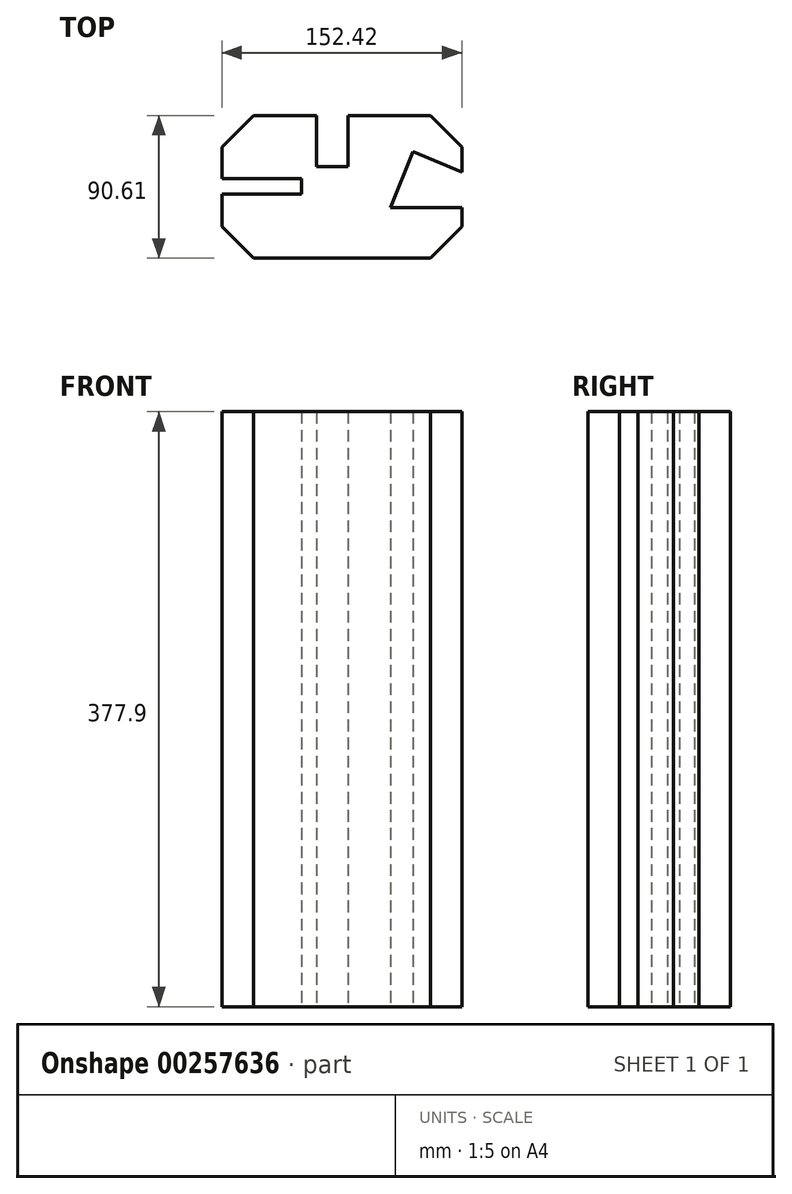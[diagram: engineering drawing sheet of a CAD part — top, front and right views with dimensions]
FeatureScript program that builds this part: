
annotation { "Feature Type Name" : "Feature", "Feature Type Description" : "" }
export const myFeature = defineFeature(function(context is Context, id is Id, definition is map)
    precondition{}
    {
        {
            var Q0;
            Q0=qCreatedBy(makeId("Top.planeOp"),FACE);
            var sketch = newSketch(context, id + "F0", { "sketchPlane" : qUnion([Q0])});
            skLineSegment(sketch, "E0", {"start": v(-44.72, -55.3) * mm, "end": v(67.68, -55.3) * mm});
            skLineSegment(sketch, "E1", {"start": v(67.68, -55.3) * mm, "end": v(87.7, -35.28) * mm});
            skLineSegment(sketch, "E2", {"start": v(-44.72, -55.3) * mm, "end": v(-64.73, -35.28) * mm});
            skLineSegment(sketch, "E3", {"start": v(87.7, -35.28) * mm, "end": v(87.7, -23.28) * mm});
            skLineSegment(sketch, "E4", {"start": v(87.7, -23.28) * mm, "end": v(42.4, -23.28) * mm});
            skLineSegment(sketch, "E5", {"start": v(42.4, -23.28) * mm, "end": v(56.81, 12.41) * mm});
            skLineSegment(sketch, "E6", {"start": v(56.81, 12.41) * mm, "end": v(87.7, -0.7) * mm});
            skLineSegment(sketch, "E7", {"start": v(87.7, -0.7) * mm, "end": v(87.7, 15.3) * mm});
            skLineSegment(sketch, "E8", {"start": v(87.7, 15.3) * mm, "end": v(67.68, 35.32) * mm});
            skLineSegment(sketch, "E9", {"start": v(67.68, 35.32) * mm, "end": v(15.28, 35.32) * mm});
            skLineSegment(sketch, "E10", {"start": v(15.28, 35.32) * mm, "end": v(15.28, 3.02) * mm});
            skLineSegment(sketch, "E11", {"start": v(15.28, 3.02) * mm, "end": v(-4.72, 3.02) * mm});
            skLineSegment(sketch, "E12", {"start": v(-4.72, 3.02) * mm, "end": v(-4.72, 35.32) * mm});
            skLineSegment(sketch, "E13", {"start": v(-4.72, 35.32) * mm, "end": v(-44.72, 35.32) * mm});
            skLineSegment(sketch, "E14", {"start": v(-44.72, 35.32) * mm, "end": v(-64.73, 15.3) * mm});
            skLineSegment(sketch, "E15", {"start": v(-64.73, 15.3) * mm, "end": v(-64.73, -4.7) * mm});
            skLineSegment(sketch, "E16", {"start": v(-64.73, -4.7) * mm, "end": v(-14.23, -4.7) * mm});
            skLineSegment(sketch, "E17", {"start": v(-14.23, -4.7) * mm, "end": v(-14.23, -14.7) * mm});
            skLineSegment(sketch, "E18", {"start": v(-14.23, -14.7) * mm, "end": v(-64.73, -14.7) * mm});
            skLineSegment(sketch, "E19", {"start": v(-64.73, -15.28) * mm, "end": v(-64.73, -35.28) * mm});
            skLineSegment(sketch, "E20", {"start": v(-64.73, -14.7) * mm, "end": v(-64.73, -15.28) * mm});
            skSolve(sketch);
        }
        {
            var Q0;
            Q0=makeQuery(id+"F0.imprint","IMPRINT",FACE,{"disambiguationData":[TD([[makeQuery(id+"F0.imprint","IMPRINT",EDGE,{"derivedFrom":sQuery(id+"F0.wireOp",EDGE,"E0")}),1.0]])]});
            extrude(context, id + "F1", {"entities" : qUnion([Q0]), "depth" : 377.9 * mm});
        }
    });
